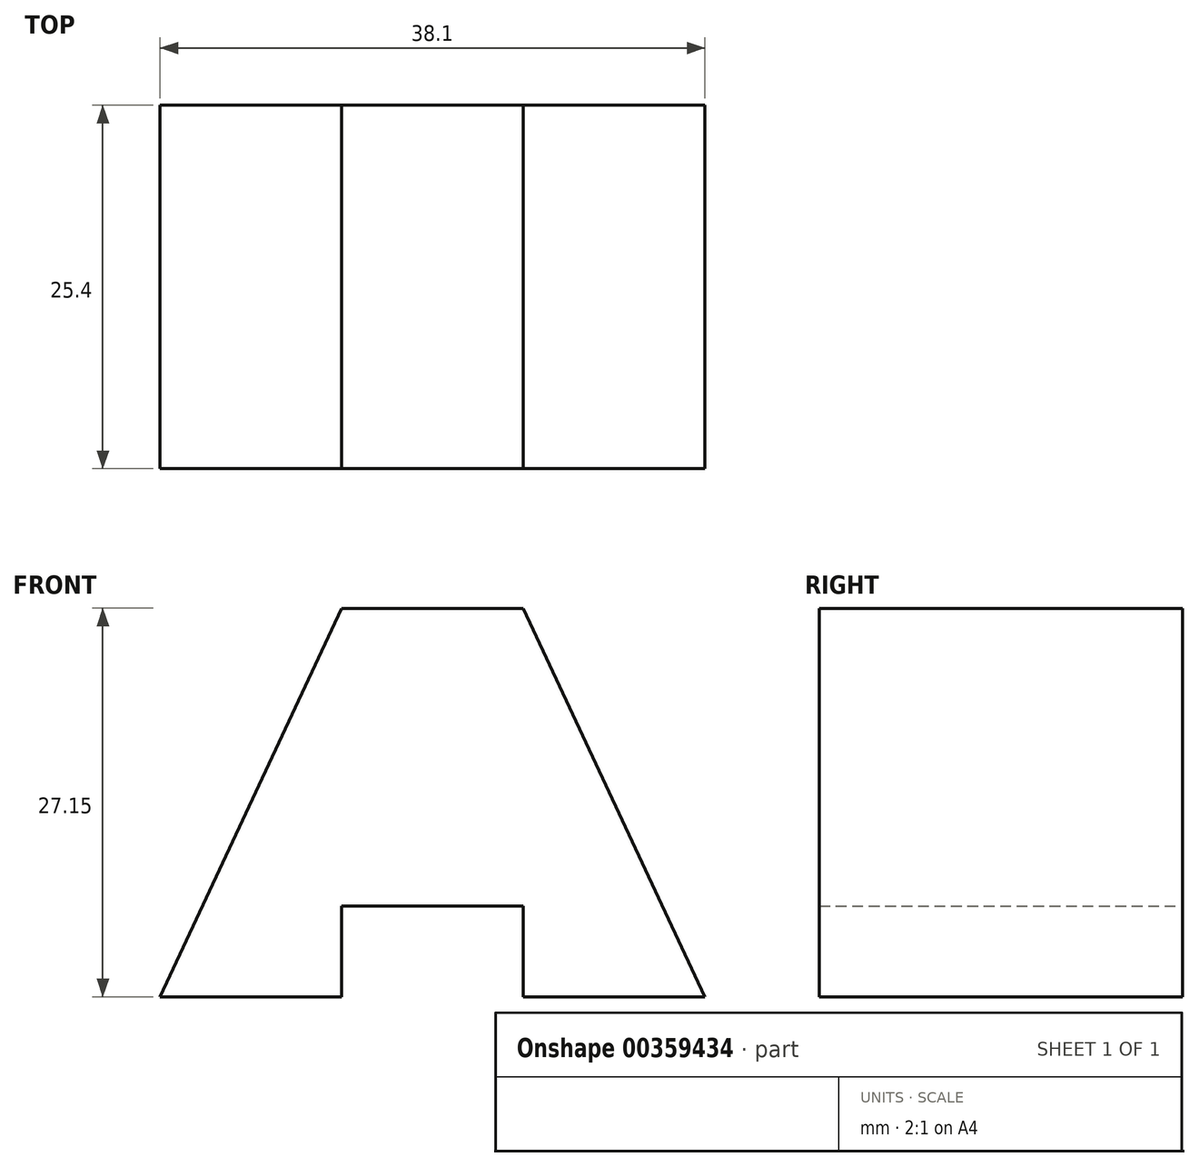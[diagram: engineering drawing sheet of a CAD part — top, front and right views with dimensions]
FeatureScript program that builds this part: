
annotation { "Feature Type Name" : "Feature", "Feature Type Description" : "" }
export const myFeature = defineFeature(function(context is Context, id is Id, definition is map)
    precondition{}
    {
        {
            var Q0;
            Q0=qCreatedBy(makeId("Front.planeOp"),FACE);
            var sketch = newSketch(context, id + "F0", { "sketchPlane" : qUnion([Q0])});
            skLineSegment(sketch, "E0", {"start": v(0, 0) * mm, "end": v(12.7, 0) * mm});
            skLineSegment(sketch, "E1", {"start": v(12.7, 0) * mm, "end": v(12.7, 6.35) * mm});
            skLineSegment(sketch, "E2", {"start": v(12.7, 6.35) * mm, "end": v(25.4, 6.35) * mm});
            skLineSegment(sketch, "E3", {"start": v(25.4, 6.35) * mm, "end": v(25.4, 0) * mm});
            skLineSegment(sketch, "E4", {"start": v(25.4, 0) * mm, "end": v(38.1, 0) * mm});
            skLineSegment(sketch, "E5", {"start": v(38.1, 0) * mm, "end": v(25.4, 27.15) * mm});
            skLineSegment(sketch, "E6", {"start": v(25.4, 27.15) * mm, "end": v(12.7, 27.15) * mm});
            skLineSegment(sketch, "E7", {"start": v(12.7, 27.15) * mm, "end": v(0, 0) * mm});
            skSolve(sketch);
        }
        {
            var Q0;
            Q0=makeQuery(id+"F0.imprint","IMPRINT",FACE,{"disambiguationData":[TD([[makeQuery(id+"F0.imprint","IMPRINT",EDGE,{"derivedFrom":sQuery(id+"F0.wireOp",EDGE,"E0")}),1.0]])]});
            extrude(context, id + "F1", {"entities" : qUnion([Q0]), "depth" : 25.4 * mm});
        }
    });
